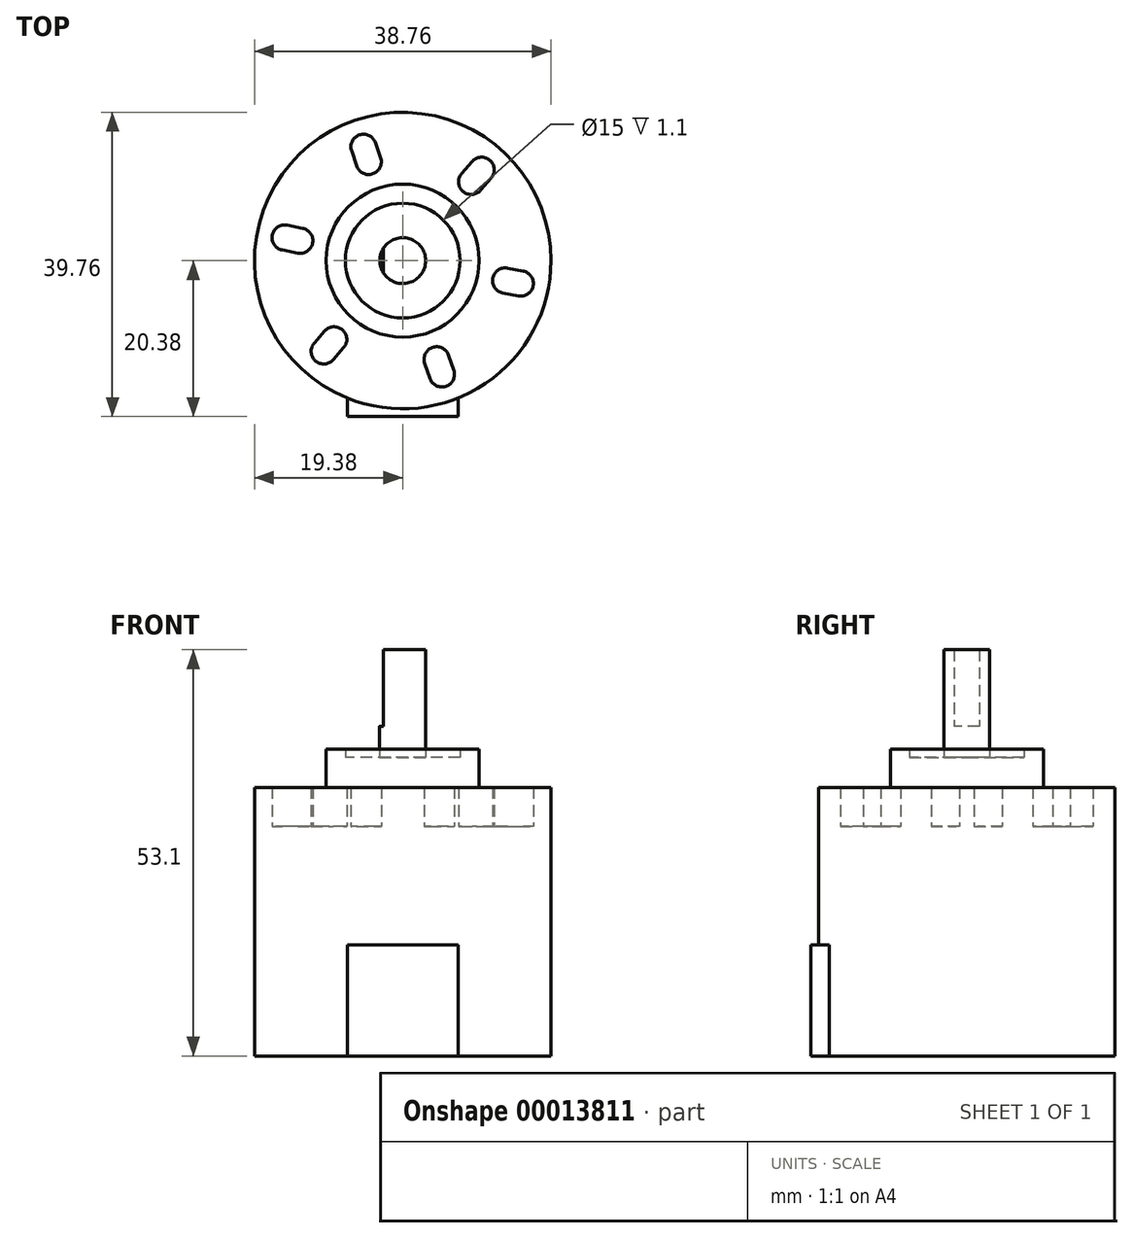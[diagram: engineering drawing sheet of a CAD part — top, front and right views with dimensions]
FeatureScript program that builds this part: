
annotation { "Feature Type Name" : "Feature", "Feature Type Description" : "" }
export const myFeature = defineFeature(function(context is Context, id is Id, definition is map)
    precondition{}
    {
        {
            var Q0;
            Q0=qCreatedBy(makeId("Top.planeOp"),FACE);
            var sketch = newSketch(context, id + "F0", { "sketchPlane" : qUnion([Q0])});
            skCircle(sketch, "E0", {"center": v(0, 0) * mm, "radius": 19.38 * mm});
            skCircle(sketch, "E1", {"center": v(0, 0) * mm, "radius": 10 * mm});
            skCircle(sketch, "E2", {"center": v(0, 0) * mm, "radius": 3 * mm});
            skLineSegment(sketch, "E3", {"start": v(-2.5, 1.66) * mm, "end": v(-2.5, -1.66) * mm});
            skCircle(sketch, "E4", {"center": v(0, 0) * mm, "radius": 7.5 * mm});
            skCircle(sketch, "E5", {"center": v(0, 0) * mm, "radius": 17.38 * mm, "construction": true});
            skCircle(sketch, "E6", {"center": v(0, 0) * mm, "radius": 12 * mm, "construction": true});
            skLineSegment(sketch, "E7", {"start": v(0, -19.38) * mm, "end": v(0, -20.38) * mm, "construction": true});
            skLineSegment(sketch, "E8", {"start": v(7.25, -17.97) * mm, "end": v(7.25, -20.38) * mm});
            skLineSegment(sketch, "E9", {"start": v(-7.25, -17.97) * mm, "end": v(-7.25, -20.38) * mm});
            skLineSegment(sketch, "E10", {"start": v(-7.25, -20.38) * mm, "end": v(0, -20.38) * mm});
            skLineSegment(sketch, "E11", {"start": v(7.25, -20.38) * mm, "end": v(0, -20.38) * mm});
            skLineSegment(sketch, "E12", {"start": v(3.9, -11.35) * mm, "end": v(5.66, -16.43) * mm, "construction": true});
            skArc(sketch, "E13", {"start": v(3.56, -15.4) * mm, "mid": v(5.66, -16.43) * mm, "end": v(6.68, -14.33) * mm});
            skArc(sketch, "E14", {"start": v(6, -12.37) * mm, "mid": v(3.9, -11.35) * mm, "end": v(2.88, -13.44) * mm});
            skLineSegment(sketch, "E15", {"start": v(2.88, -13.44) * mm, "end": v(3.56, -15.4) * mm});
            skLineSegment(sketch, "E16", {"start": v(6, -12.37) * mm, "end": v(6.68, -14.33) * mm});
            skLineSegment(sketch, "E17.1.0", {"start": v(13.71, -0.98) * mm, "end": v(15.75, -1.38) * mm});
            skArc(sketch, "E17.1.1", {"start": v(13.71, -0.98) * mm, "mid": v(11.78, -2.29) * mm, "end": v(13.08, -4.22) * mm});
            skLineSegment(sketch, "E17.1.2", {"start": v(13.08, -4.22) * mm, "end": v(15.12, -4.62) * mm});
            skArc(sketch, "E17.1.3", {"start": v(15.12, -4.62) * mm, "mid": v(17.06, -3.32) * mm, "end": v(15.75, -1.38) * mm});
            skLineSegment(sketch, "E17.2.0", {"start": v(7.7, 11.38) * mm, "end": v(9.07, 12.95) * mm});
            skArc(sketch, "E17.2.1", {"start": v(7.7, 11.38) * mm, "mid": v(7.87, 9.06) * mm, "end": v(10.2, 9.22) * mm});
            skLineSegment(sketch, "E17.2.2", {"start": v(10.2, 9.22) * mm, "end": v(11.56, 10.79) * mm});
            skArc(sketch, "E17.2.3", {"start": v(11.56, 10.79) * mm, "mid": v(11.4, 13.11) * mm, "end": v(9.07, 12.95) * mm});
            skLineSegment(sketch, "E17.3.0", {"start": v(-6, 12.37) * mm, "end": v(-6.68, 14.33) * mm});
            skArc(sketch, "E17.3.1", {"start": v(-6, 12.37) * mm, "mid": v(-3.9, 11.35) * mm, "end": v(-2.88, 13.44) * mm});
            skLineSegment(sketch, "E17.3.2", {"start": v(-2.88, 13.44) * mm, "end": v(-3.56, 15.4) * mm});
            skArc(sketch, "E17.3.3", {"start": v(-3.56, 15.4) * mm, "mid": v(-5.66, 16.43) * mm, "end": v(-6.68, 14.33) * mm});
            skLineSegment(sketch, "E17.4.0", {"start": v(-13.71, 0.98) * mm, "end": v(-15.75, 1.38) * mm});
            skArc(sketch, "E17.4.1", {"start": v(-13.71, 0.98) * mm, "mid": v(-11.78, 2.29) * mm, "end": v(-13.08, 4.22) * mm});
            skLineSegment(sketch, "E17.4.2", {"start": v(-13.08, 4.22) * mm, "end": v(-15.12, 4.62) * mm});
            skArc(sketch, "E17.4.3", {"start": v(-15.12, 4.62) * mm, "mid": v(-17.06, 3.32) * mm, "end": v(-15.75, 1.38) * mm});
            skLineSegment(sketch, "E17.5.0", {"start": v(-7.7, -11.38) * mm, "end": v(-9.07, -12.95) * mm});
            skArc(sketch, "E17.5.1", {"start": v(-7.7, -11.38) * mm, "mid": v(-7.87, -9.06) * mm, "end": v(-10.2, -9.22) * mm});
            skLineSegment(sketch, "E17.5.2", {"start": v(-10.2, -9.22) * mm, "end": v(-11.56, -10.79) * mm});
            skArc(sketch, "E17.5.3", {"start": v(-11.56, -10.79) * mm, "mid": v(-11.4, -13.11) * mm, "end": v(-9.07, -12.95) * mm});
            skSolve(sketch);
        }
        {
            var Q0;
            Q0=makeQuery(id+"F0.imprint","IMPRINT",FACE,{"disambiguationData":[TD([[makeQuery(id+"F0.imprint","IMPRINT",EDGE,{"derivedFrom":sQuery(id+"F0.wireOp",EDGE,"E1")}),1.0]])]});
            extrude(context, id + "F1", {"entities" : qUnion([Q0]), "depth" : 40.1 * mm});
        }
        {
            var Q0;
            Q0=makeQuery(id+"F0.imprint","IMPRINT",FACE,{"disambiguationData":[TD([[makeQuery(id+"F0.imprint","IMPRINT",EDGE,{"derivedFrom":sQuery(id+"F0.wireOp",EDGE,"E4")}),1.0]])]});
            extrude(context, id + "F2", {"entities" : qUnion([Q0]), "operationType" : NewBodyOperationType.ADD, "depth" : 39 * mm});
        }
        {
            var Q0;
            {var subQ0=sQuery(id+"F0.wireOp",EDGE,"E3");Q0=makeQuery(id+"F0.imprint","IMPRINT",FACE,{"disambiguationData":[TD([[makeQuery(id+"F0.imprint","IMPRINT",EDGE,{"derivedFrom":subQ0}),-1.0]])]});}
            extrude(context, id + "F3", {"entities" : qUnion([Q0]), "operationType" : NewBodyOperationType.ADD, "depth" : 43.1 * mm});
        }
        {
            var Q0;
            {var subQ0=sQuery(id+"F0.wireOp",EDGE,"E3");Q0=makeQuery(id+"F0.imprint","IMPRINT",FACE,{"disambiguationData":[TD([[makeQuery(id+"F0.imprint","IMPRINT",EDGE,{"derivedFrom":subQ0}),1.0]])]});}
            extrude(context, id + "F4", {"entities" : qUnion([Q0]), "operationType" : NewBodyOperationType.ADD, "depth" : 53.1 * mm});
        }
        {
            var Q0;
            Q0=makeQuery(id+"F0.imprint","IMPRINT",FACE,{"disambiguationData":[TD([[makeQuery(id+"F0.imprint","IMPRINT",EDGE,{"derivedFrom":sQuery(id+"F0.wireOp",EDGE,"E1")}),-1.0]])]});
            extrude(context, id + "F5", {"entities" : qUnion([Q0]), "operationType" : NewBodyOperationType.ADD, "depth" : 35.1 * mm});
        }
        {
            var Q0;
            {var subQ1=sQuery(id+"F0.wireOp",EDGE,"E8");Q0=makeQuery(id+"F0.imprint","IMPRINT",FACE,{"disambiguationData":[TD([[makeQuery(id+"F0.imprint","IMPRINT",EDGE,{"derivedFrom":subQ1}),-1.0]])]});}
            extrude(context, id + "F6", {"entities" : qUnion([Q0]), "operationType" : NewBodyOperationType.ADD, "depth" : 14.5 * mm});
        }
        {
            var Q0;
            Q0=makeQuery(id+"F0.imprint","IMPRINT",FACE,{"disambiguationData":[TD([[makeQuery(id+"F0.imprint","IMPRINT",EDGE,{"derivedFrom":sQuery(id+"F0.wireOp",EDGE,"E13")}),1.0]])]});
            var Q1;
            Q1=makeQuery(id+"F0.imprint","IMPRINT",FACE,{"disambiguationData":[TD([[makeQuery(id+"F0.imprint","IMPRINT",EDGE,{"derivedFrom":sQuery(id+"F0.wireOp",EDGE,"E17.5.0")}),-1.0]])]});
            var Q2;
            Q2=makeQuery(id+"F0.imprint","IMPRINT",FACE,{"disambiguationData":[TD([[makeQuery(id+"F0.imprint","IMPRINT",EDGE,{"derivedFrom":sQuery(id+"F0.wireOp",EDGE,"E17.4.0")}),-1.0]])]});
            var Q3;
            Q3=makeQuery(id+"F0.imprint","IMPRINT",FACE,{"disambiguationData":[TD([[makeQuery(id+"F0.imprint","IMPRINT",EDGE,{"derivedFrom":sQuery(id+"F0.wireOp",EDGE,"E17.3.0")}),-1.0]])]});
            var Q4;
            Q4=makeQuery(id+"F0.imprint","IMPRINT",FACE,{"disambiguationData":[TD([[makeQuery(id+"F0.imprint","IMPRINT",EDGE,{"derivedFrom":sQuery(id+"F0.wireOp",EDGE,"E17.2.0")}),-1.0]])]});
            var Q5;
            Q5=makeQuery(id+"F0.imprint","IMPRINT",FACE,{"disambiguationData":[TD([[makeQuery(id+"F0.imprint","IMPRINT",EDGE,{"derivedFrom":sQuery(id+"F0.wireOp",EDGE,"E17.1.0")}),-1.0]])]});
            extrude(context, id + "F7", {"entities" : qUnion([Q0, Q1, Q2, Q3, Q4, Q5]), "operationType" : NewBodyOperationType.ADD, "depth" : 30 * mm});
        }
    });
